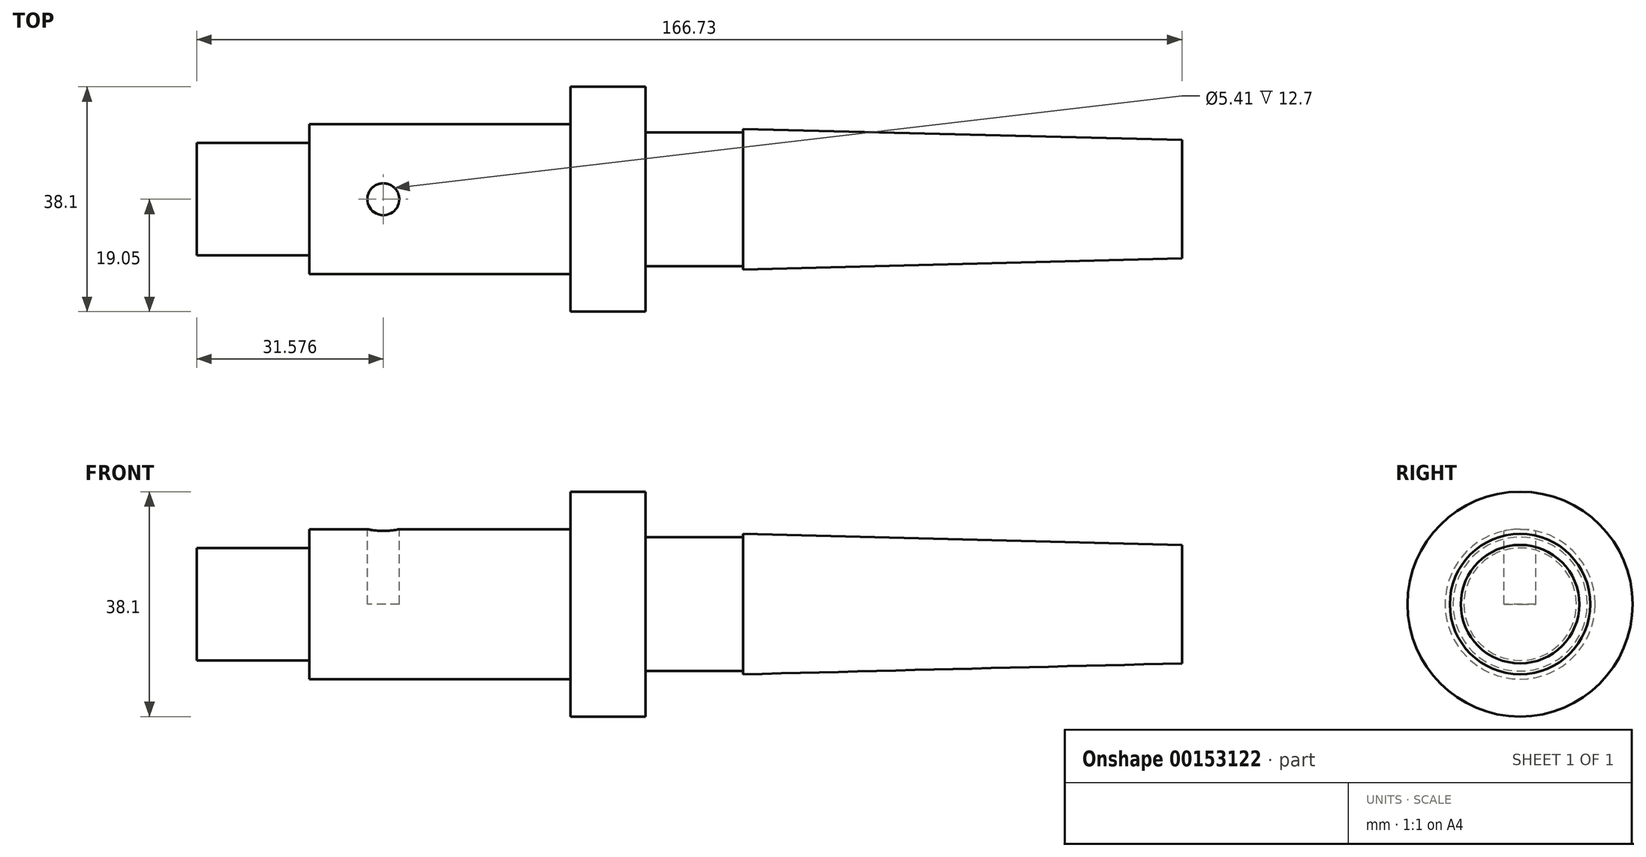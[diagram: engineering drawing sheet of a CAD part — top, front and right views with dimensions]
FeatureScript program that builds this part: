
annotation { "Feature Type Name" : "Feature", "Feature Type Description" : "" }
export const myFeature = defineFeature(function(context is Context, id is Id, definition is map)
    precondition{}
    {
        {
            var Q0;
            Q0=qCreatedBy(makeId("Right.planeOp"),FACE);
            var sketch = newSketch(context, id + "F0", { "sketchPlane" : qUnion([Q0])});
            skCircle(sketch, "E0", {"center": v(0, 0) * mm, "radius": 19.05 * mm});
            skSolve(sketch);
        }
        {
            var Q0;
            Q0=makeQuery(id+"F0.imprint","IMPRINT",FACE,{"disambiguationData":[TD([[makeQuery(id+"F0.imprint","IMPRINT",EDGE,{"derivedFrom":sQuery(id+"F0.wireOp",EDGE,"E0")}),1.0]])]});
            extrude(context, id + "F1", {"entities" : qUnion([Q0]), "depth" : 12.7 * mm});
        }
        {
            var Q0;
            Q0=makeQuery(id+"F1.opExtrude","CAP_FACE",FACE,{"disambiguationData":[OSD([sQuery(id+"F0.wireOp",EDGE,"E0")])],"isStart":true});
            var sketch = newSketch(context, id + "F2", { "sketchPlane" : qUnion([Q0])});
            skCircle(sketch, "E1", {"center": v(0, 0) * mm, "radius": 12.7 * mm});
            skSolve(sketch);
        }
        {
            var Q0;
            Q0=makeQuery(id+"F2.imprint","IMPRINT",FACE,{"disambiguationData":[TD([[makeQuery(id+"F2.imprint","IMPRINT",EDGE,{"derivedFrom":sQuery(id+"F2.wireOp",EDGE,"E1")}),1.0]])]});
            extrude(context, id + "F3", {"entities" : qUnion([Q0]), "operationType" : NewBodyOperationType.ADD, "depth" : 44.2 * mm});
        }
        {
            var Q0;
            Q0=makeQuery(id+"F3.opExtrude","CAP_FACE",FACE,{"disambiguationData":[OSD([sQuery(id+"F2.wireOp",EDGE,"E1")])],"isStart":false});
            var sketch = newSketch(context, id + "F4", { "sketchPlane" : qUnion([Q0])});
            skCircle(sketch, "E2", {"center": v(0, 0) * mm, "radius": 9.53 * mm});
            skSolve(sketch);
        }
        {
            var Q0;
            Q0=makeQuery(id+"F4.imprint","IMPRINT",FACE,{"disambiguationData":[TD([[makeQuery(id+"F4.imprint","IMPRINT",EDGE,{"derivedFrom":sQuery(id+"F4.wireOp",EDGE,"E2")}),1.0]])]});
            extrude(context, id + "F5", {"entities" : qUnion([Q0]), "operationType" : NewBodyOperationType.ADD, "depth" : 19.05 * mm});
        }
        {
            var Q0;
            Q0=makeQuery(id+"F1.opExtrude","CAP_FACE",FACE,{"disambiguationData":[OSD([sQuery(id+"F0.wireOp",EDGE,"E0")])],"isStart":false});
            var sketch = newSketch(context, id + "F6", { "sketchPlane" : qUnion([Q0])});
            skCircle(sketch, "E3", {"center": v(0, 0) * mm, "radius": 11.35 * mm});
            skSolve(sketch);
        }
        {
            var Q0;
            Q0=makeQuery(id+"F6.imprint","IMPRINT",FACE,{"disambiguationData":[TD([[makeQuery(id+"F6.imprint","IMPRINT",EDGE,{"derivedFrom":sQuery(id+"F6.wireOp",EDGE,"E3")}),1.0]])]});
            extrude(context, id + "F7", {"entities" : qUnion([Q0]), "operationType" : NewBodyOperationType.ADD, "depth" : 16.5 * mm});
        }
        {
            var Q0;
            Q0=makeQuery(id+"F7.opExtrude","CAP_FACE",FACE,{"disambiguationData":[OSD([sQuery(id+"F6.wireOp",EDGE,"E3")])],"isStart":false});
            var sketch = newSketch(context, id + "F8", { "sketchPlane" : qUnion([Q0])});
            skCircle(sketch, "E4", {"center": v(0, 0) * mm, "radius": 11.89 * mm});
            skSolve(sketch);
        }
        {
            var Q0;
            Q0=makeQuery(id+"F8.imprint","IMPRINT",FACE,{"disambiguationData":[TD([[makeQuery(id+"F8.imprint","IMPRINT",EDGE,{"derivedFrom":makeQuery(id+"F7.opExtrude","CAP_EDGE",EDGE,{"disambiguationData":[OSD([sQuery(id+"F6.wireOp",EDGE,"E3")])],"isStart":false})}),1.0]])]});
            var Q1;
            Q1=makeQuery(id+"F8.imprint","IMPRINT",FACE,{"disambiguationData":[TD([[makeQuery(id+"F8.imprint","IMPRINT",EDGE,{"derivedFrom":sQuery(id+"F8.wireOp",EDGE,"E4")}),1.0]])]});
            extrude(context, id + "F9", {"entities" : qUnion([Q0, Q1]), "operationType" : NewBodyOperationType.ADD, "depth" : 74.27 * mm, "hasDraft" : true, "draftAngle" : 1.43 * degree, "draftPullDirection" : true});
        }
        {
            var Q0;
            Q0=qCreatedBy(makeId("Top.planeOp"),FACE);
            cPlane(context, id + "F10", {"entities" : qUnion([Q0]), "cplaneType" : CPlaneType.OFFSET, "offset" : 12.7 * mm, "width" : 152.4 * mm, "height" : 152.4 * mm});
        }
        {
            var Q0;
            Q0=qCreatedBy(id+"F10.planeOp",FACE);
            var sketch = newSketch(context, id + "F11", { "sketchPlane" : qUnion([Q0])});
            skLineSegment(sketch, "E5", {"start": v(0, 0) * mm, "end": v(-31.67, 0) * mm});
            skCircle(sketch, "E6", {"center": v(-31.67, 0) * mm, "radius": 2.7 * mm});
            skSolve(sketch);
        }
        {
            var Q0;
            Q0=makeQuery(id+"F11.imprint","IMPRINT",FACE,{"disambiguationData":[TD([[makeQuery(id+"F11.imprint","IMPRINT",EDGE,{"derivedFrom":sQuery(id+"F11.wireOp",EDGE,"E6")}),1.0]])]});
            extrude(context, id + "F12", {"entities" : qUnion([Q0]), "operationType" : NewBodyOperationType.REMOVE, "oppositeDirection" : true, "depth" : 12.7 * mm});
        }
    });
